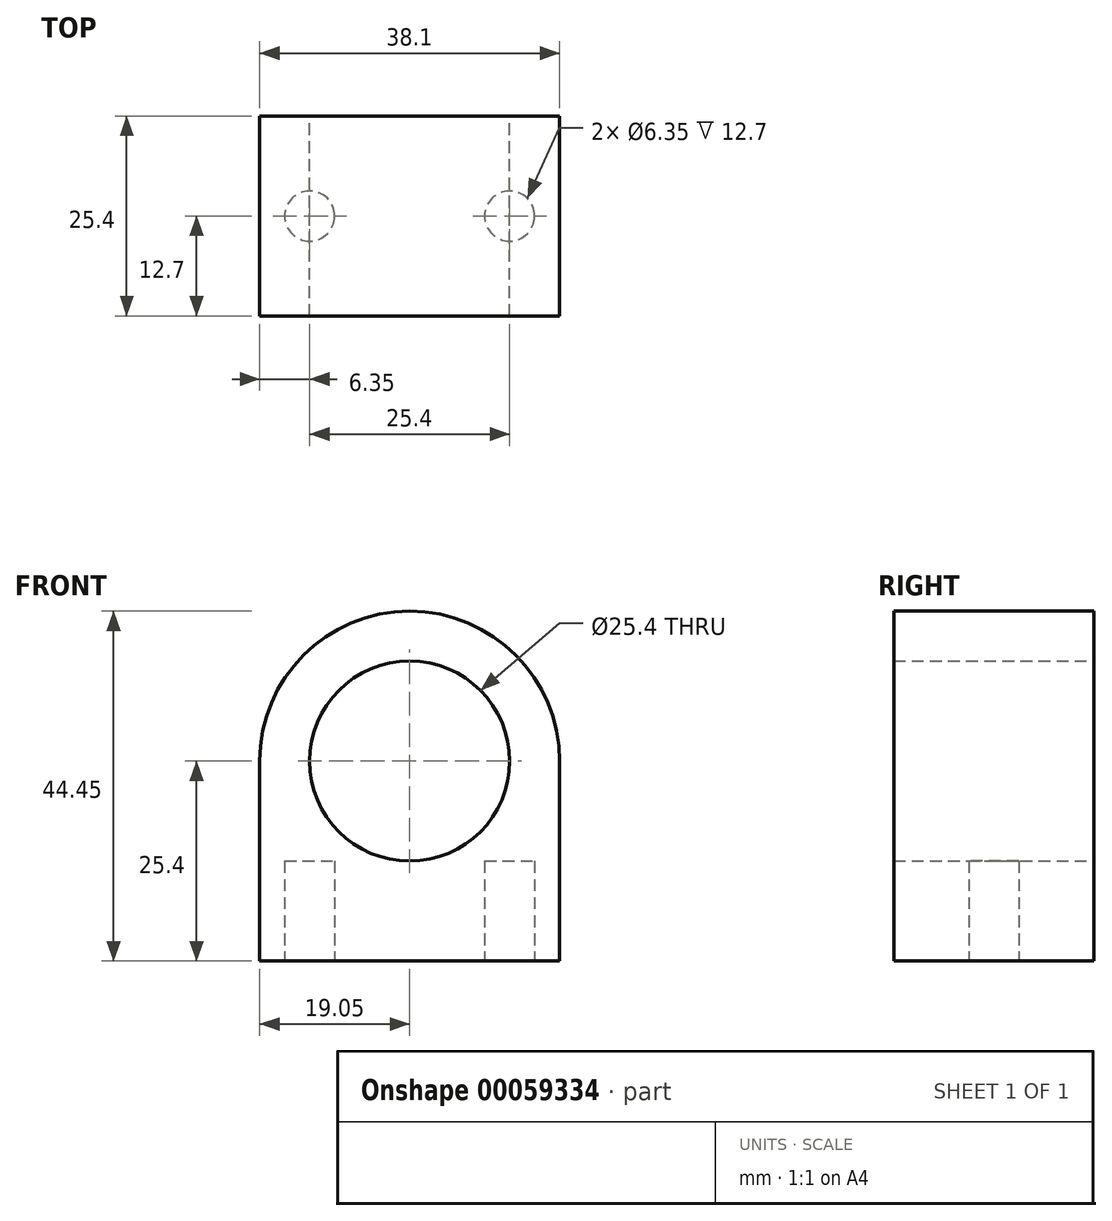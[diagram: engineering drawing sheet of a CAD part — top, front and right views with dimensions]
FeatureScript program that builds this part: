
annotation { "Feature Type Name" : "Feature", "Feature Type Description" : "" }
export const myFeature = defineFeature(function(context is Context, id is Id, definition is map)
    precondition{}
    {
        {
            var Q0;
            Q0=qCreatedBy(makeId("Front.planeOp"),FACE);
            var sketch = newSketch(context, id + "F0", { "sketchPlane" : qUnion([Q0])});
            skArc(sketch, "E0", {"start": v(19.05, 0) * mm, "mid": v(0, 19.05) * mm, "end": v(-19.05, 0) * mm});
            skLineSegment(sketch, "E1", {"start": v(-19.05, 0) * mm, "end": v(-19.05, -25.4) * mm});
            skLineSegment(sketch, "E2", {"start": v(-19.05, -25.4) * mm, "end": v(19.05, -25.4) * mm});
            skLineSegment(sketch, "E3", {"start": v(19.05, 0) * mm, "end": v(19.05, -25.4) * mm});
            skCircle(sketch, "E4", {"center": v(0, 0) * mm, "radius": 12.7 * mm});
            skSolve(sketch);
        }
        {
            var Q0;
            Q0 = qSketchRegion(id + "F0", true);
            extrude(context, id + "F1", {"entities" : qUnion([Q0]), "endBound" : BoundingType.SYMMETRIC, "offsetDistance" : 25.4 * mm, "depth" : 25.4 * mm});
        }
        {
            var Q0;
            Q0=makeQuery(id+"F1.opExtrude","SWEPT_FACE",FACE,{"disambiguationData":[OSD([sQuery(id+"F0.wireOp",EDGE,"E2")])]});
            var sketch = newSketch(context, id + "F2", { "sketchPlane" : qUnion([Q0])});
            skCircle(sketch, "E5", {"center": v(-12.7, 0) * mm, "radius": 3.18 * mm});
            skCircle(sketch, "E6.MirrorC", {"center": v(12.7, 0) * mm, "radius": 3.18 * mm});
            skSolve(sketch);
        }
        {
            var Q0;
            Q0 = qSketchRegion(id + "F2", true);
            extrude(context, id + "F3", {"entities" : qUnion([Q0]), "operationType" : NewBodyOperationType.REMOVE, "oppositeDirection" : true, "offsetDistance" : 25.4 * mm, "depth" : 12.7 * mm});
        }
    });
